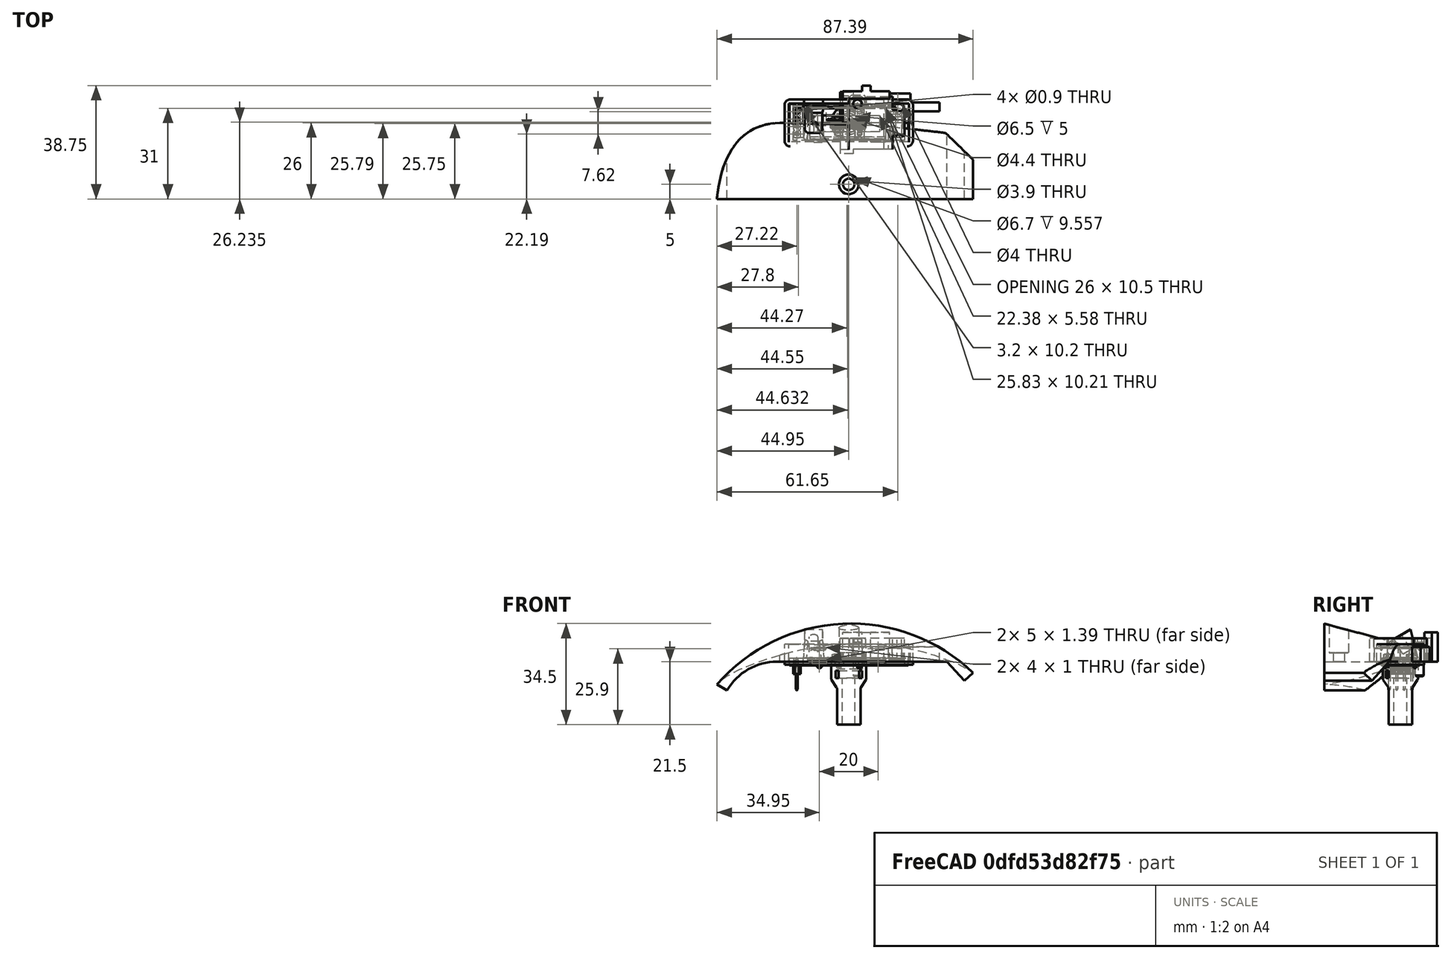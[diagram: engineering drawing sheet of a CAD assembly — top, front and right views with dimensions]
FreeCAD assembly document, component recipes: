
FREECAD ASSEMBLY — COMPONENT RECIPES ("replicazeron")

This assembly document has 16 components, labeled P0..P15 below (a component is one placed body or linked part). 0 of them carry a construction recipe — the FreeCAD feature program that regenerates the part from scratch, quoted from this document or its linked companion documents; the rest are supplied as boundary geometry only. No exploded tour is included for this assembly.
COMPONENT P0 — geometry summary ("0603 Capacitor_001"; no construction recipe available for this part):
  bounding box: 1.6 x 1.0 x 0.8 mm
  tessellated surface: 12 triangles
  volume: 1 mm^3 (100% of its bounding box)
  symmetry: mirror-symmetric across its x mid-plane
COMPONENT P1 — geometry summary ("0603 Capacitor_002"; no construction recipe available for this part):
  bounding box: 1.6 x 1.0 x 0.8 mm
  tessellated surface: 12 triangles
  volume: 1 mm^3 (100% of its bounding box)
  symmetry: mirror-symmetric across its x mid-plane
COMPONENT P2 — geometry summary ("0603 Capacitor_003"; no construction recipe available for this part):
  bounding box: 1.6 x 1.0 x 0.8 mm
  tessellated surface: 12 triangles
  volume: 1 mm^3 (100% of its bounding box)
  symmetry: mirror-symmetric across its x mid-plane
COMPONENT P3 — geometry summary ("0603 Capacitor_004"; no construction recipe available for this part):
  bounding box: 1.6 x 1.0 x 0.8 mm
  tessellated surface: 12 triangles
  volume: 1 mm^3 (100% of its bounding box)
  symmetry: mirror-symmetric across its x mid-plane
COMPONENT P4 — geometry summary ("0603 Capacitor_005"; no construction recipe available for this part):
  bounding box: 1.6 x 1.0 x 0.8 mm
  tessellated surface: 12 triangles
  volume: 1 mm^3 (100% of its bounding box)
  symmetry: mirror-symmetric across its x mid-plane
COMPONENT P5 — geometry summary ("0603 Capacitor_006"; no construction recipe available for this part):
  bounding box: 1.6 x 1.0 x 0.8 mm
  tessellated surface: 12 triangles
  volume: 1 mm^3 (100% of its bounding box)
  symmetry: mirror-symmetric across its x mid-plane
COMPONENT P6 — geometry summary ("0603 Capacitor_007"; no construction recipe available for this part):
  bounding box: 1.6 x 1.0 x 0.8 mm
  tessellated surface: 12 triangles
  volume: 1 mm^3 (100% of its bounding box)
  symmetry: mirror-symmetric across its x mid-plane
COMPONENT P7 — geometry summary ("0603 Capacitor_008"; no construction recipe available for this part):
  bounding box: 1.6 x 1.0 x 0.8 mm
  tessellated surface: 12 triangles
  volume: 1 mm^3 (100% of its bounding box)
  symmetry: mirror-symmetric across its x mid-plane
COMPONENT P8 — geometry summary ("0603 Resistor_001"; no construction recipe available for this part):
  bounding box: 1.6 x 0.8 x 0.5 mm
  tessellated surface: 12 triangles
  volume: 1 mm^3 (100% of its bounding box)
  symmetry: mirror-symmetric across its x mid-plane
COMPONENT P9 — geometry summary ("0603 Resistor_002"; no construction recipe available for this part):
  bounding box: 1.6 x 0.8 x 0.5 mm
  tessellated surface: 12 triangles
  volume: 1 mm^3 (100% of its bounding box)
  symmetry: mirror-symmetric across its x mid-plane
COMPONENT P10 — geometry summary ("0603 Resistor_003"; no construction recipe available for this part):
  bounding box: 1.6 x 0.8 x 0.5 mm
  tessellated surface: 12 triangles
  volume: 1 mm^3 (100% of its bounding box)
  symmetry: mirror-symmetric across its x mid-plane
COMPONENT P11 — geometry summary ("0603 Resistor_004"; no construction recipe available for this part):
  bounding box: 1.6 x 0.8 x 0.5 mm
  tessellated surface: 12 triangles
  volume: 1 mm^3 (100% of its bounding box)
  symmetry: mirror-symmetric across its x mid-plane
COMPONENT P12 — geometry summary ("0603 Resistor_005"; no construction recipe available for this part):
  bounding box: 1.6 x 0.8 x 0.5 mm
  tessellated surface: 12 triangles
  volume: 1 mm^3 (100% of its bounding box)
  symmetry: mirror-symmetric across its x mid-plane
COMPONENT P13 — geometry summary ("1x4 Male Header_001"; no construction recipe available for this part):
  bounding box: 11.2 x 10.2 x 2.5 mm
  tessellated surface: 15,836 triangles
  volume: 87 mm^3 (30% of its bounding box)
  symmetry: 2-fold rotationally symmetric about the z axis; mirror-symmetric across its x mid-plane, y mid-plane
COMPONENT P14 — geometry summary ("Board_001"; no construction recipe available for this part):
  bounding box: 38.0 x 12.0 x 2.6 mm
  tessellated surface: 6,006 triangles
  volume: 1012 mm^3 (85% of its bounding box)
COMPONENT P15 — geometry summary ("Surface Mount Transistor_001"; no construction recipe available for this part):
  bounding box: 2.9 x 2.5 x 1.0 mm
  tessellated surface: 856 triangles
  volume: 3 mm^3 (46% of its bounding box)
  symmetry: mirror-symmetric across its y mid-plane
PROVENANCE & LICENSES
A FreeCAD (.FCStd) document from a public repository crawl; recipes are the document's own serialized feature recipes (and, for linked parts, companion documents' recipes).
License: as declared in the source repository (recorded in the dataset sidecar).
